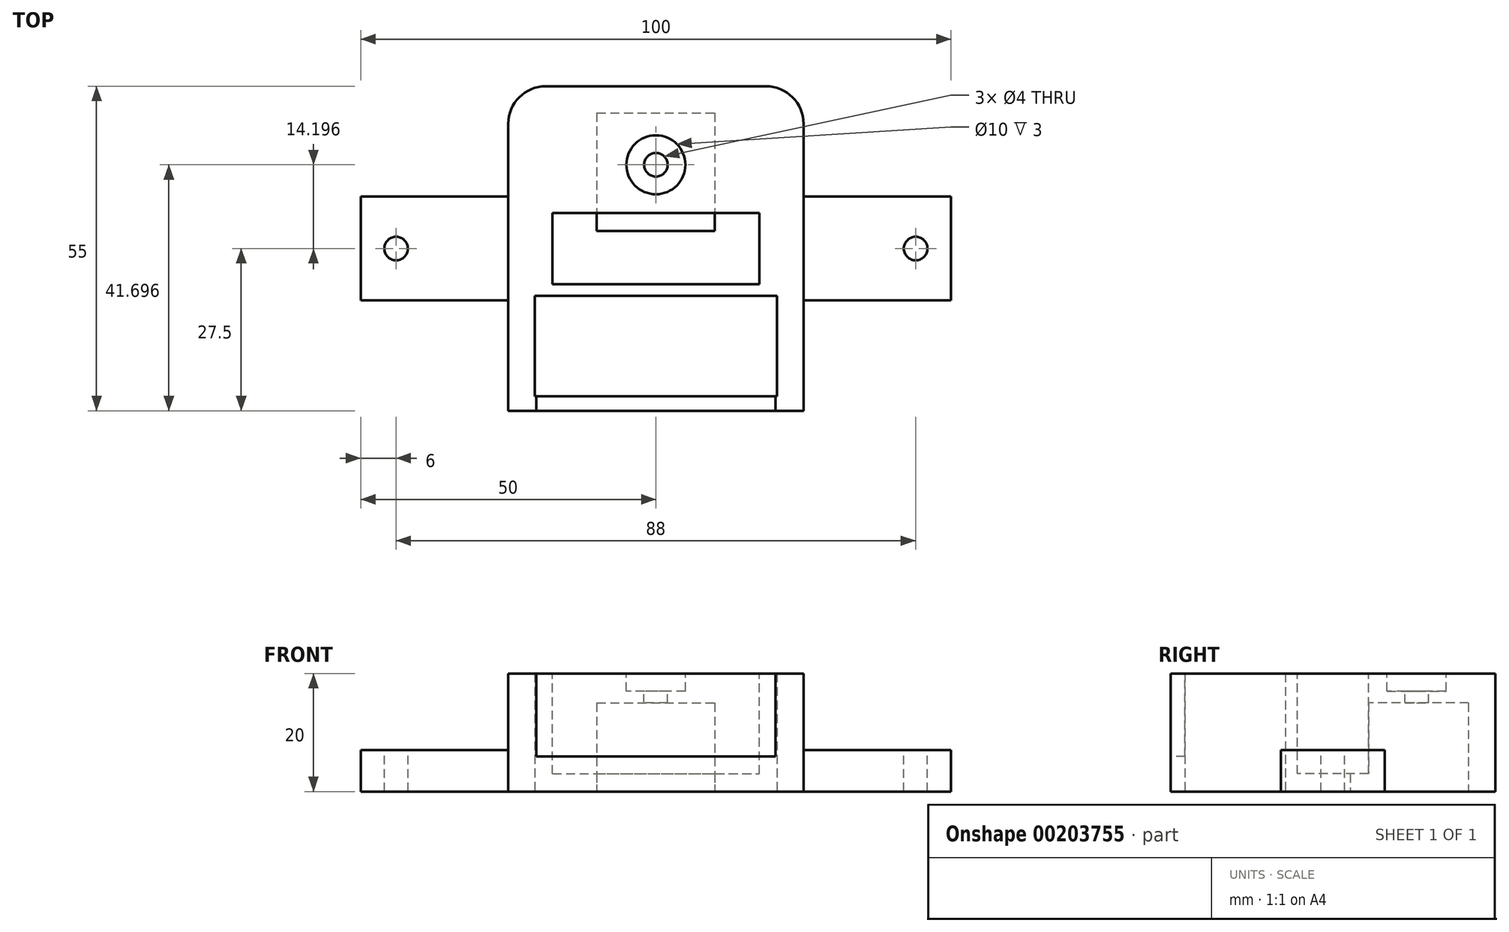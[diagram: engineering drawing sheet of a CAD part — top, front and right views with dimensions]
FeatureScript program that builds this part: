
annotation { "Feature Type Name" : "Feature", "Feature Type Description" : "" }
export const myFeature = defineFeature(function(context is Context, id is Id, definition is map)
    precondition{}
    {
        {
            var Q0;
            Q0=qCreatedBy(makeId("Top.planeOp"),FACE);
            var sketch = newSketch(context, id + "F0", { "sketchPlane" : qUnion([Q0])});
            skLineSegment(sketch, "E0.bottom", {"start": v(-25, -27.5) * mm, "end": v(25, -27.5) * mm});
            skLineSegment(sketch, "E0.top", {"start": v(-18.65, 27.5) * mm, "end": v(18.65, 27.5) * mm});
            skLineSegment(sketch, "E0.left", {"start": v(-25, -27.5) * mm, "end": v(-25, 21.15) * mm});
            skLineSegment(sketch, "E0.right", {"start": v(25, -27.5) * mm, "end": v(25, 21.15) * mm});
            skPoint(sketch, "E0.middle", {"position": v(0, 0) * mm});
            skPoint(sketch, "E1.visualSharp", {"position": v(-25, 27.5) * mm});
            skArc(sketch, "E1.filletArc", {"start": v(-18.65, 27.5) * mm, "mid": v(-23.14, 25.64) * mm, "end": v(-25, 21.15) * mm});
            skPoint(sketch, "E2.visualSharp", {"position": v(25, 27.5) * mm});
            skArc(sketch, "E2.filletArc", {"start": v(25, 21.15) * mm, "mid": v(23.14, 25.64) * mm, "end": v(18.65, 27.5) * mm});
            skLineSegment(sketch, "E3.bottom", {"start": v(-10, 22.96) * mm, "end": v(10, 22.96) * mm});
            skLineSegment(sketch, "E3.top", {"start": v(-10, 2.96) * mm, "end": v(10, 2.96) * mm});
            skLineSegment(sketch, "E3.left", {"start": v(-10, 22.96) * mm, "end": v(-10, 2.96) * mm});
            skLineSegment(sketch, "E3.right", {"start": v(10, 22.96) * mm, "end": v(10, 2.96) * mm});
            skPoint(sketch, "E3.middle", {"position": v(0, 12.96) * mm});
            skLineSegment(sketch, "E4.bottom", {"start": v(-20.5, -25.04) * mm, "end": v(20.5, -25.04) * mm});
            skLineSegment(sketch, "E4.top", {"start": v(-20.5, -8.04) * mm, "end": v(20.5, -8.04) * mm});
            skLineSegment(sketch, "E4.left", {"start": v(-20.5, -25.04) * mm, "end": v(-20.5, -8.04) * mm});
            skLineSegment(sketch, "E4.right", {"start": v(20.5, -25.04) * mm, "end": v(20.5, -8.04) * mm});
            skPoint(sketch, "E4.middle", {"position": v(0, -16.54) * mm});
            skPoint(sketch, "E4.middle.positionSnap0", {"position": v(0, -27.5) * mm});
            skPoint(sketch, "E4.centerSnap0", {"position": v(0, -27.5) * mm});
            skSolve(sketch);
        }
        {
            var Q0;
            Q0 = qSketchRegion(id + "F0", true);
            extrude(context, id + "F1", {"entities" : qUnion([Q0]), "depth" : 20 * mm});
        }
        {
            var Q0;
            Q0=makeQuery(id+"F1.opExtrude","SWEPT_FACE",FACE,{"disambiguationData":[OSD([sQuery(id+"F0.wireOp",EDGE,"E0.bottom")])]});
            var sketch = newSketch(context, id + "F2", { "sketchPlane" : qUnion([Q0])});
            skLineSegment(sketch, "E5.bottom", {"start": v(20.26, 20) * mm, "end": v(-20.26, 20) * mm});
            skLineSegment(sketch, "E5.top", {"start": v(20.26, 5.93) * mm, "end": v(-20.26, 5.93) * mm});
            skLineSegment(sketch, "E5.left", {"start": v(20.26, 20) * mm, "end": v(20.26, 5.93) * mm});
            skLineSegment(sketch, "E5.right", {"start": v(-20.26, 20) * mm, "end": v(-20.26, 5.93) * mm});
            skPoint(sketch, "E5.middle", {"position": v(0, 12.96) * mm});
            skSolve(sketch);
        }
        {
            var Q0;
            Q0=makeQuery(id+"F2.imprint","IMPRINT",FACE,{"disambiguationData":[TD([[makeQuery(id+"F2.imprint","IMPRINT",EDGE,{"derivedFrom":sQuery(id+"F2.wireOp",EDGE,"E5.bottom")}),-1.0]])]});
            extrude(context, id + "F3", {"entities" : qUnion([Q0]), "operationType" : NewBodyOperationType.REMOVE, "oppositeDirection" : true, "depth" : 5 * mm});
        }
        {
            var Q0;
            Q0=makeQuery(id+"F1.opExtrude","CAP_FACE",FACE,{"disambiguationData":[OSD([sQuery(id+"F0.wireOp",EDGE,"E0.bottom"),sQuery(id+"F0.wireOp",EDGE,"E0.top"),sQuery(id+"F0.wireOp",EDGE,"E0.left"),sQuery(id+"F0.wireOp",EDGE,"E0.right"),sQuery(id+"F0.wireOp",EDGE,"E1.filletArc"),sQuery(id+"F0.wireOp",EDGE,"E2.filletArc"),sQuery(id+"F0.wireOp",EDGE,"E3.bottom"),sQuery(id+"F0.wireOp",EDGE,"E3.top"),sQuery(id+"F0.wireOp",EDGE,"E3.left"),sQuery(id+"F0.wireOp",EDGE,"E3.right"),sQuery(id+"F0.wireOp",EDGE,"E4.bottom"),sQuery(id+"F0.wireOp",EDGE,"E4.top"),sQuery(id+"F0.wireOp",EDGE,"E4.left"),sQuery(id+"F0.wireOp",EDGE,"E4.right")])],"isStart":true});
            var sketch = newSketch(context, id + "F4", { "sketchPlane" : qUnion([Q0])});
            skPoint(sketch, "E6", {"position": v(25, 0) * mm});
            skPoint(sketch, "E7", {"position": v(50, 0) * mm});
            skPoint(sketch, "E8", {"position": v(-25, 0) * mm});
            skPoint(sketch, "E9", {"position": v(-50, 0) * mm});
            skPoint(sketch, "E10", {"position": v(-37.5, 0) * mm});
            skPoint(sketch, "E11", {"position": v(37.5, 0) * mm});
            skLineSegment(sketch, "E12.bottom", {"start": v(-50, 8.8) * mm, "end": v(-25, 8.8) * mm});
            skLineSegment(sketch, "E12.top", {"start": v(-50, -8.8) * mm, "end": v(-25, -8.8) * mm});
            skLineSegment(sketch, "E12.left", {"start": v(-50, 8.8) * mm, "end": v(-50, -8.8) * mm});
            skLineSegment(sketch, "E12.right", {"start": v(-25, 8.8) * mm, "end": v(-25, -8.8) * mm});
            skLineSegment(sketch, "E13.bottom", {"start": v(25, 8.8) * mm, "end": v(50, 8.8) * mm});
            skLineSegment(sketch, "E13.top", {"start": v(25, -8.8) * mm, "end": v(50, -8.8) * mm});
            skLineSegment(sketch, "E13.left", {"start": v(25, 8.8) * mm, "end": v(25, -8.8) * mm});
            skLineSegment(sketch, "E13.right", {"start": v(50, 8.8) * mm, "end": v(50, -8.8) * mm});
            skSolve(sketch);
        }
        {
            var Q0;
            Q0 = qSketchRegion(id + "F4", true);
            extrude(context, id + "F5", {"entities" : qUnion([Q0]), "operationType" : NewBodyOperationType.ADD, "oppositeDirection" : true, "depth" : 7 * mm});
        }
        {
            var Q0;
            Q0=makeQuery(id+"F1.opExtrude","CAP_FACE",FACE,{"disambiguationData":[OSD([sQuery(id+"F0.wireOp",EDGE,"E0.bottom"),sQuery(id+"F0.wireOp",EDGE,"E0.top"),sQuery(id+"F0.wireOp",EDGE,"E0.left"),sQuery(id+"F0.wireOp",EDGE,"E0.right"),sQuery(id+"F0.wireOp",EDGE,"E1.filletArc"),sQuery(id+"F0.wireOp",EDGE,"E2.filletArc"),sQuery(id+"F0.wireOp",EDGE,"E3.bottom"),sQuery(id+"F0.wireOp",EDGE,"E3.top"),sQuery(id+"F0.wireOp",EDGE,"E3.left"),sQuery(id+"F0.wireOp",EDGE,"E3.right"),sQuery(id+"F0.wireOp",EDGE,"E4.bottom"),sQuery(id+"F0.wireOp",EDGE,"E4.top"),sQuery(id+"F0.wireOp",EDGE,"E4.left"),sQuery(id+"F0.wireOp",EDGE,"E4.right")])],"isStart":false});
            var sketch = newSketch(context, id + "F6", { "sketchPlane" : qUnion([Q0])});
            skLineSegment(sketch, "E14.bottom", {"start": v(-10, 22.96) * mm, "end": v(10, 22.96) * mm});
            skLineSegment(sketch, "E14.top", {"start": v(-10, 2.96) * mm, "end": v(10, 2.96) * mm});
            skLineSegment(sketch, "E14.left", {"start": v(-10, 22.96) * mm, "end": v(-10, 2.96) * mm});
            skLineSegment(sketch, "E14.right", {"start": v(10, 22.96) * mm, "end": v(10, 2.96) * mm});
            skSolve(sketch);
        }
        {
            var Q0;
            Q0=makeQuery(id+"F6.imprint","IMPRINT",FACE,{"disambiguationData":[TD([[makeQuery(id+"F6.imprint","IMPRINT",EDGE,{"derivedFrom":sQuery(id+"F6.wireOp",EDGE,"E14.bottom")}),-1.0]])]});
            extrude(context, id + "F7", {"entities" : qUnion([Q0]), "operationType" : NewBodyOperationType.ADD, "oppositeDirection" : true, "depth" : 5 * mm});
        }
        {
            var Q0;
            Q0=makeQuery(id+"F7.boolean.opBoolean","MERGE",FACE,{"derivedFrom":[makeQuery(id+"F1.opExtrude","CAP_FACE",FACE,{"disambiguationData":[OSD([sQuery(id+"F0.wireOp",EDGE,"E0.bottom"),sQuery(id+"F0.wireOp",EDGE,"E0.top"),sQuery(id+"F0.wireOp",EDGE,"E0.left"),sQuery(id+"F0.wireOp",EDGE,"E0.right"),sQuery(id+"F0.wireOp",EDGE,"E1.filletArc"),sQuery(id+"F0.wireOp",EDGE,"E2.filletArc"),sQuery(id+"F0.wireOp",EDGE,"E3.bottom"),sQuery(id+"F0.wireOp",EDGE,"E3.top"),sQuery(id+"F0.wireOp",EDGE,"E3.left"),sQuery(id+"F0.wireOp",EDGE,"E3.right"),sQuery(id+"F0.wireOp",EDGE,"E4.bottom"),sQuery(id+"F0.wireOp",EDGE,"E4.top"),sQuery(id+"F0.wireOp",EDGE,"E4.left"),sQuery(id+"F0.wireOp",EDGE,"E4.right")])],"isStart":false}),makeQuery(id+"F7.opExtrude","CAP_FACE",FACE,{"disambiguationData":[OSD([sQuery(id+"F6.wireOp",EDGE,"E14.bottom"),sQuery(id+"F6.wireOp",EDGE,"E14.top"),sQuery(id+"F6.wireOp",EDGE,"E14.left"),sQuery(id+"F6.wireOp",EDGE,"E14.right")])],"isStart":true})]});
            var sketch = newSketch(context, id + "F8", { "sketchPlane" : qUnion([Q0])});
            skCircle(sketch, "E15", {"center": v(0, 14.2) * mm, "radius": 2 * mm});
            skSolve(sketch);
        }
        {
            var Q0;
            Q0 = qSketchRegion(id + "F8", true);
            extrude(context, id + "F9", {"entities" : qUnion([Q0]), "operationType" : NewBodyOperationType.REMOVE, "oppositeDirection" : true, "depth" : 10 * mm});
        }
        {
            var Q0;
            Q0=makeQuery(id+"F7.boolean.opBoolean","MERGE",FACE,{"derivedFrom":[makeQuery(id+"F1.opExtrude","CAP_FACE",FACE,{"disambiguationData":[OSD([sQuery(id+"F0.wireOp",EDGE,"E0.bottom"),sQuery(id+"F0.wireOp",EDGE,"E0.top"),sQuery(id+"F0.wireOp",EDGE,"E0.left"),sQuery(id+"F0.wireOp",EDGE,"E0.right"),sQuery(id+"F0.wireOp",EDGE,"E1.filletArc"),sQuery(id+"F0.wireOp",EDGE,"E2.filletArc"),sQuery(id+"F0.wireOp",EDGE,"E3.bottom"),sQuery(id+"F0.wireOp",EDGE,"E3.top"),sQuery(id+"F0.wireOp",EDGE,"E3.left"),sQuery(id+"F0.wireOp",EDGE,"E3.right"),sQuery(id+"F0.wireOp",EDGE,"E4.bottom"),sQuery(id+"F0.wireOp",EDGE,"E4.top"),sQuery(id+"F0.wireOp",EDGE,"E4.left"),sQuery(id+"F0.wireOp",EDGE,"E4.right")])],"isStart":false}),makeQuery(id+"F7.opExtrude","CAP_FACE",FACE,{"disambiguationData":[OSD([sQuery(id+"F6.wireOp",EDGE,"E14.bottom"),sQuery(id+"F6.wireOp",EDGE,"E14.top"),sQuery(id+"F6.wireOp",EDGE,"E14.left"),sQuery(id+"F6.wireOp",EDGE,"E14.right")])],"isStart":true})]});
            var sketch = newSketch(context, id + "F10", { "sketchPlane" : qUnion([Q0])});
            skCircle(sketch, "E16", {"center": v(0, 14.2) * mm, "radius": 5 * mm});
            skSolve(sketch);
        }
        {
            var Q0;
            Q0 = qSketchRegion(id + "F10", true);
            extrude(context, id + "F11", {"entities" : qUnion([Q0]), "operationType" : NewBodyOperationType.REMOVE, "oppositeDirection" : true, "depth" : 3 * mm});
        }
        {
            var Q0;
            Q0=makeQuery(id+"F7.boolean.opBoolean","MERGE",FACE,{"derivedFrom":[makeQuery(id+"F1.opExtrude","CAP_FACE",FACE,{"disambiguationData":[OSD([sQuery(id+"F0.wireOp",EDGE,"E0.bottom"),sQuery(id+"F0.wireOp",EDGE,"E0.top"),sQuery(id+"F0.wireOp",EDGE,"E0.left"),sQuery(id+"F0.wireOp",EDGE,"E0.right"),sQuery(id+"F0.wireOp",EDGE,"E1.filletArc"),sQuery(id+"F0.wireOp",EDGE,"E2.filletArc"),sQuery(id+"F0.wireOp",EDGE,"E3.bottom"),sQuery(id+"F0.wireOp",EDGE,"E3.top"),sQuery(id+"F0.wireOp",EDGE,"E3.left"),sQuery(id+"F0.wireOp",EDGE,"E3.right"),sQuery(id+"F0.wireOp",EDGE,"E4.bottom"),sQuery(id+"F0.wireOp",EDGE,"E4.top"),sQuery(id+"F0.wireOp",EDGE,"E4.left"),sQuery(id+"F0.wireOp",EDGE,"E4.right")])],"isStart":false}),makeQuery(id+"F7.opExtrude","CAP_FACE",FACE,{"disambiguationData":[OSD([sQuery(id+"F6.wireOp",EDGE,"E14.bottom"),sQuery(id+"F6.wireOp",EDGE,"E14.top"),sQuery(id+"F6.wireOp",EDGE,"E14.left"),sQuery(id+"F6.wireOp",EDGE,"E14.right")])],"isStart":true})]});
            var sketch = newSketch(context, id + "F12", { "sketchPlane" : qUnion([Q0])});
            skLineSegment(sketch, "E17.bottom", {"start": v(-17.5, 6.04) * mm, "end": v(17.5, 6.04) * mm});
            skLineSegment(sketch, "E17.top", {"start": v(-17.5, -6.04) * mm, "end": v(17.5, -6.04) * mm});
            skLineSegment(sketch, "E17.left", {"start": v(-17.5, 6.04) * mm, "end": v(-17.5, -6.04) * mm});
            skLineSegment(sketch, "E17.right", {"start": v(17.5, 6.04) * mm, "end": v(17.5, -6.04) * mm});
            skPoint(sketch, "E17.middle", {"position": v(0, 0) * mm});
            skSolve(sketch);
        }
        {
            var Q0;
            Q0=makeQuery(id+"F12.imprint","IMPRINT",FACE,{"disambiguationData":[TD([[makeQuery(id+"F12.imprint","IMPRINT",EDGE,{"derivedFrom":sQuery(id+"F12.wireOp",EDGE,"E17.bottom")}),-1.0]])]});
            var Q1;
            Q1 = qConstructionFilter(qBodyType(qCreatedBy(id + "F12" ,EDGE), BodyType.WIRE), ConstructionObject.NO);
            extrude(context, id + "F13", {"entities" : qUnion([Q0]), "operationType" : NewBodyOperationType.REMOVE, "surfaceEntities" : qUnion([Q1]), "oppositeDirection" : true, "depth" : 17 * mm});
        }
        {
            var Q0;
            Q0=makeQuery(id+"F5.opExtrude","CAP_FACE",FACE,{"disambiguationData":[OSD([sQuery(id+"F4.wireOp",EDGE,"E12.bottom"),sQuery(id+"F4.wireOp",EDGE,"E12.top"),sQuery(id+"F4.wireOp",EDGE,"E12.left"),sQuery(id+"F4.wireOp",EDGE,"E12.right")])],"isStart":false});
            var sketch = newSketch(context, id + "F14", { "sketchPlane" : qUnion([Q0])});
            skCircle(sketch, "E18", {"center": v(-44, 0) * mm, "radius": 2 * mm});
            skCircle(sketch, "E19", {"center": v(44, 0) * mm, "radius": 2 * mm});
            skSolve(sketch);
        }
        {
            var Q0;
            Q0 = qSketchRegion(id + "F14", true);
            extrude(context, id + "F15", {"entities" : qUnion([Q0]), "operationType" : NewBodyOperationType.REMOVE, "oppositeDirection" : true, "depth" : 10 * mm});
        }
    });
